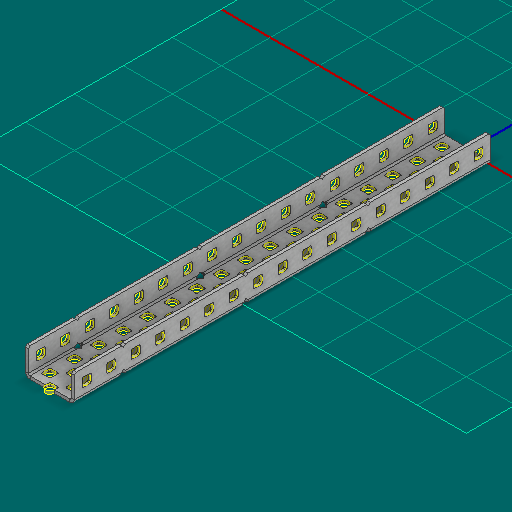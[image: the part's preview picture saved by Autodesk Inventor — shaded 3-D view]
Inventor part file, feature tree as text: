
AUTODESK INVENTOR PART (.ipt)
format: ipt  version: 2025 (Build 290162000, 162)  size: 1,497,088 bytes
history: native  units: in
note: dims shown in document units (in); Inventor stores cm internally (conversion verified against a paired STEP export)
features: other x176, sketch x5, sheet_metal_op x1
ambient origin geometry x8: Origin, YZ Plane, XZ Plane, XY Plane, X Axis, Y Axis, Z Axis, Center Point
bodies: Solid1 (feature_tree)
feature tree (182):
  other  "Alu C 1x2x1x17.ipt"
  other  "Solid1::Alu C 1x2x1x17.ipt"
  other  "TaggingFeature1"
  sketch  "Sketch1"  dims[d0=0.3937in]
  sketch  "Sketch2"  dims[d1=0.0625in]
  sketch  "Sketch3"
  other  "Flange Pattern Sketch"
  sketch  "Sketch9"
  sheet_metal_op  "Body Pattern Sketch"
  other  "Arc Length"
  sketch  "Sketch14"
  other  "Flange Pattern Plane"
  other  "Srf1"
  other  "Srf2"
  other  "Srf3"
  other  "Srf4"
  other  "Srf5"
  other  "Srf6"
  other  "Srf7"
  other  "Srf8"
  other  "Srf9"
  other  "Srf10"
  other  "Srf11"
  other  "Srf12"
  other  "Srf13"
  other  "Srf14"
  other  "Srf15"
  other  "Srf16"
  other  "Srf17"
  other  "Srf18"
  other  "Srf19"
  other  "Srf20"
  other  "Srf21"
  other  "Srf22"
  other  "Srf23"
  other  "Srf24"
  other  "Srf25"
  other  "Srf26"
  other  "Srf27"
  other  "Srf28"
  other  "Srf29"
  other  "Srf30"
  other  "Srf31"
  other  "Srf32"
  other  "Srf33"
  other  "Srf34"
  other  "Srf35"
  other  "Srf36"
  other  "Srf37"
  other  "Srf38"
  other  "Srf39"
  other  "Srf40"
  other  "Srf41"
  other  "Srf42"
  other  "Srf43"
  other  "Srf44"
  other  "Srf45"
  other  "Srf46"
  other  "Srf47"
  other  "Srf48"
  other  "Srf49"
  other  "Srf50"
  other  "Srf51"
  other  "Srf52"
  other  "Srf53"
  other  "Srf54"
  other  "Srf55"
  other  "Srf56"
  other  "Srf57"
  other  "Srf58"
  other  "Srf59"
  other  "Srf60"
  other  "Srf61"
  other  "Srf62"
  other  "Srf63"
  other  "Srf64"
  other  "Srf65"
  other  "Srf66"
  other  "Srf67"
  other  "Srf68"
  other  "Srf69"
  other  "Srf70"
  other  "Srf71"
  other  "Srf72"
  other  "Srf73"
  other  "Srf74"
  other  "Srf75"
  other  "Srf76"
  other  "Srf77"
  other  "Srf78"
  other  "Srf79"
  other  "Srf80"
  other  "Srf81"
  other  "Srf82"
  other  "Srf83"
  other  "Srf84"
  other  "Srf85"
  other  "Srf1::Derived"
  other  "Srf2::Derived"
  other  "Srf823::Derived"
  other  "Srf824::Derived"
  other  "Srf825::Derived"
  other  "Srf826::Derived"
  other  "Srf827::Derived"
  other  "Srf828::Derived"
  other  "Srf829::Derived"
  other  "Srf922::Derived"
  other  "Srf923::Derived"
  other  "Srf924::Derived"
  other  "Srf925::Derived"
  other  "Srf926::Derived"
  other  "Srf1143::Derived"
  other  "Srf1144::Derived"
  other  "Srf1145::Derived"
  other  "Srf1146::Derived"
  other  "Srf1147::Derived"
  other  "Srf1148::Derived"
  other  "Srf1149::Derived"
  other  "Srf1150::Derived"
  other  "Srf1151::Derived"
  other  "Srf1152::Derived"
  other  "Srf1153::Derived"
  other  "Srf1154::Derived"
  other  "Srf1155::Derived"
  other  "Srf1156::Derived"
  other  "Srf1157::Derived"
  other  "Srf1158::Derived"
  other  "Srf1159::Derived"
  other  "Srf1160::Derived"
  other  "Srf1161::Derived"
  other  "Srf1162::Derived"
  other  "Srf91::Derived"
  other  "Srf92::Derived"
  other  "Srf856::Derived"
  other  "Srf857::Derived"
  other  "Srf858::Derived"
  other  "Srf859::Derived"
  other  "Srf860::Derived"
  other  "Srf861::Derived"
  other  "Srf862::Derived"
  other  "Srf959::Derived"
  other  "Srf960::Derived"
  other  "Srf961::Derived"
  other  "Srf962::Derived"
  other  "Srf963::Derived"
  other  "Srf1199::Derived"
  other  "Srf1200::Derived"
  other  "Srf1201::Derived"
  other  "Srf1202::Derived"
  other  "Srf1203::Derived"
  other  "Srf1204::Derived"
  other  "Srf1205::Derived"
  other  "Srf1206::Derived"
  other  "Srf1207::Derived"
  other  "Srf1208::Derived"
  other  "Srf1209::Derived"
  other  "Srf1210::Derived"
  other  "Srf1211::Derived"
  other  "Srf1212::Derived"
  other  "Srf1213::Derived"
  other  "Srf1214::Derived"
  other  "Srf1215::Derived"
  other  "Srf1216::Derived"
  other  "Srf1217::Derived"
  other  "Srf1218::Derived"
  other  "Srf786::Derived"
  other  "Srf889::Derived"
  other  "Srf890::Derived"
  other  "Srf891::Derived"
  other  "Srf892::Derived"
  other  "Srf893::Derived"
  other  "Srf894::Derived"
  other  "Srf895::Derived"
  other  "Srf896::Derived"
  other  "Srf996::Derived"
  other  "Srf997::Derived"
  other  "Srf998::Derived"
  other  "Srf999::Derived"
  other  "Srf1000::Derived"
  other  "Srf1255::Derived"
  other  "Srf1256::Derived"
  other  "Srf1257::Derived"
